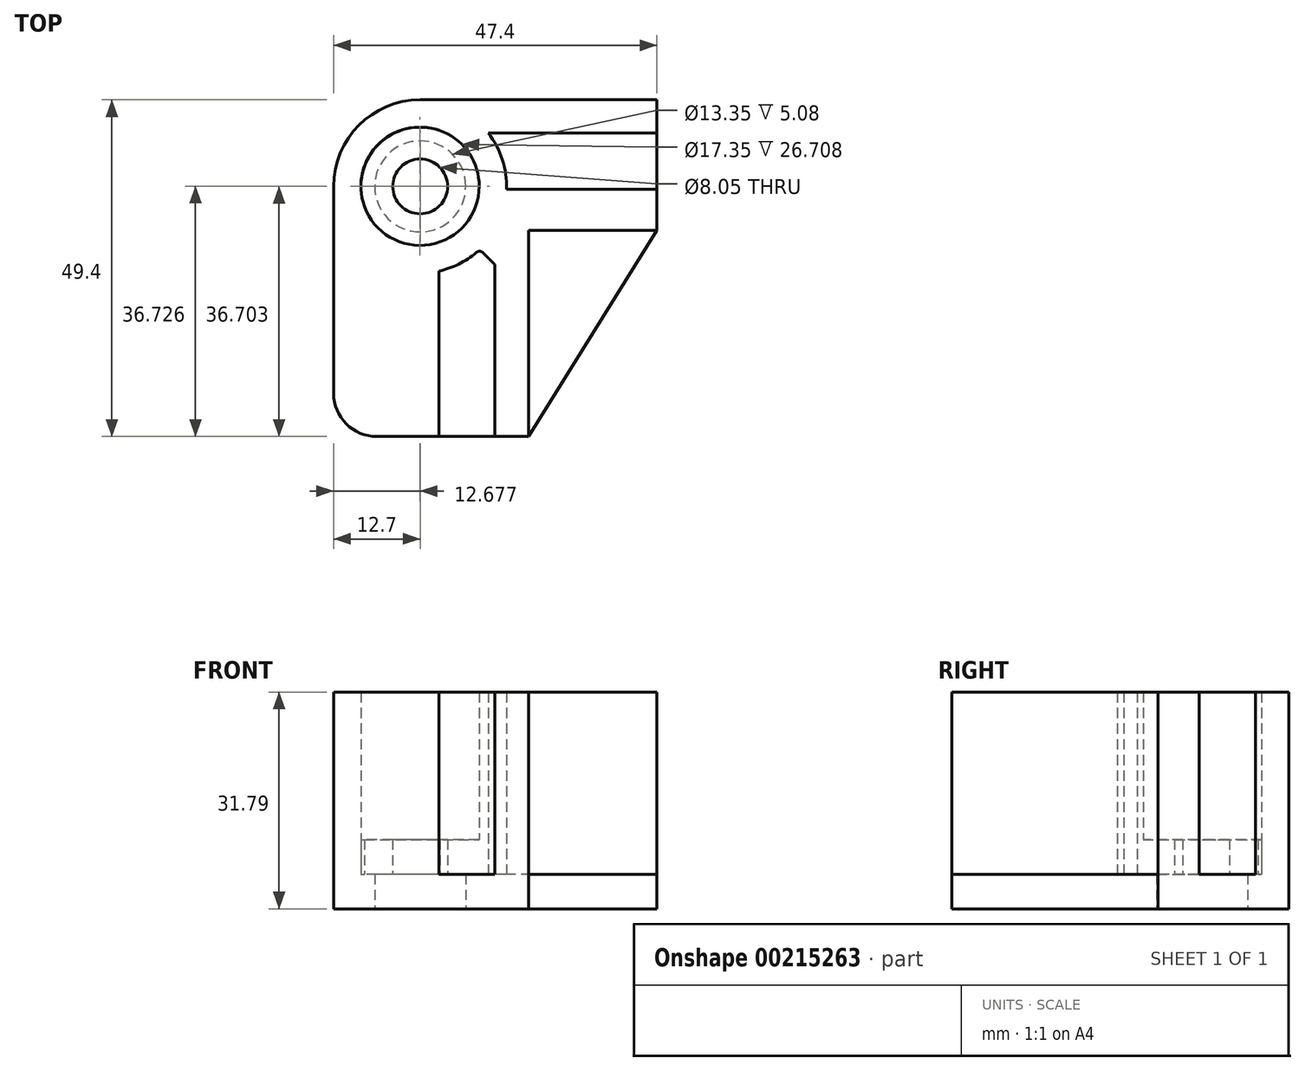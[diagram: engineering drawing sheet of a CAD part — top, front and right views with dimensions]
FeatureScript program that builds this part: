
annotation { "Feature Type Name" : "Feature", "Feature Type Description" : "" }
export const myFeature = defineFeature(function(context is Context, id is Id, definition is map)
    precondition{}
    {
        {
            var Q0;
            Q0=qCreatedBy(makeId("Top.planeOp"),FACE);
            var sketch = newSketch(context, id + "F0", { "sketchPlane" : qUnion([Q0])});
            skLineSegment(sketch, "E0.bottom", {"start": v(6.35, 0) * mm, "end": v(28.6, 0) * mm});
            skLineSegment(sketch, "E0.top", {"start": v(12.7, 49.4) * mm, "end": v(47.4, 49.4) * mm});
            skLineSegment(sketch, "E0.left", {"start": v(0, 6.35) * mm, "end": v(0, 36.7) * mm});
            skLineSegment(sketch, "E0.right", {"start": v(47.4, 30.23) * mm, "end": v(47.4, 49.4) * mm});
            skPoint(sketch, "E1", {"position": v(47.4, 30.23) * mm});
            skPoint(sketch, "E2", {"position": v(28.6, 0) * mm});
            skLineSegment(sketch, "E3", {"start": v(28.6, 0) * mm, "end": v(47.4, 30.23) * mm});
            skArc(sketch, "E4.filletArc", {"start": v(12.7, 49.4) * mm, "mid": v(3.72, 45.68) * mm, "end": v(0, 36.7) * mm});
            skArc(sketch, "E5.filletArc", {"start": v(0, 6.35) * mm, "mid": v(1.86, 1.86) * mm, "end": v(6.35, 0) * mm});
            skCircle(sketch, "E6", {"center": v(12.7, 36.7) * mm, "radius": 6.67 * mm});
            skSolve(sketch);
        }
        {
            var Q0;
            Q0=makeQuery(id+"F0.imprint","IMPRINT",FACE,{"disambiguationData":[TD([[makeQuery(id+"F0.imprint","IMPRINT",EDGE,{"derivedFrom":sQuery(id+"F0.wireOp",EDGE,"E0.bottom")}),1.0]])]});
            extrude(context, id + "F1", {"entities" : qUnion([Q0]), "depth" : 5.08 * mm});
        }
        {
            var Q0;
            Q0=makeQuery(id+"F1.opExtrude","CAP_FACE",FACE,{"disambiguationData":[OSD([sQuery(id+"F0.wireOp",EDGE,"E0.bottom"),sQuery(id+"F0.wireOp",EDGE,"E0.top"),sQuery(id+"F0.wireOp",EDGE,"E0.left"),sQuery(id+"F0.wireOp",EDGE,"E0.right"),sQuery(id+"F0.wireOp",EDGE,"E3"),sQuery(id+"F0.wireOp",EDGE,"E4.filletArc"),sQuery(id+"F0.wireOp",EDGE,"E5.filletArc"),sQuery(id+"F0.wireOp",EDGE,"E6")])],"isStart":false});
            var Q1;
            Q1=makeQuery(id+"F1.opExtrude","CAP_FACE",FACE,{"disambiguationData":[OSD([sQuery(id+"F0.wireOp",EDGE,"E0.bottom"),sQuery(id+"F0.wireOp",EDGE,"E0.top"),sQuery(id+"F0.wireOp",EDGE,"E0.left"),sQuery(id+"F0.wireOp",EDGE,"E0.right"),sQuery(id+"F0.wireOp",EDGE,"E3"),sQuery(id+"F0.wireOp",EDGE,"E4.filletArc"),sQuery(id+"F0.wireOp",EDGE,"E5.filletArc"),sQuery(id+"F0.wireOp",EDGE,"E6")])],"isStart":false});
            var Q2;
            Q2=qCreatedBy(makeId("Front.planeOp"),FACE);
            var sketch = newSketch(context, id + "F2", { "sketchPlane" : qUnion([Q0, Q1, Q2])});
            skLineSegment(sketch, "E7.bottom", {"start": v(6.35, 0) * mm, "end": v(28.6, 0) * mm});
            skLineSegment(sketch, "E7.top", {"start": v(12.7, 49.4) * mm, "end": v(47.4, 49.4) * mm});
            skLineSegment(sketch, "E7.left", {"start": v(0, 6.36) * mm, "end": v(0, 36.7) * mm});
            skLineSegment(sketch, "E7.right", {"start": v(47.4, 30.23) * mm, "end": v(47.4, 49.4) * mm});
            skPoint(sketch, "E8", {"position": v(47.4, 30.23) * mm});
            skPoint(sketch, "E9", {"position": v(28.6, 0) * mm});
            skLineSegment(sketch, "E10", {"start": v(28.6, 0) * mm, "end": v(47.4, 30.23) * mm});
            skArc(sketch, "E11.filletArc", {"start": v(0, 6.36) * mm, "mid": v(1.86, 1.87) * mm, "end": v(6.35, 0) * mm});
            skCircle(sketch, "E12", {"center": v(12.68, 36.73) * mm, "radius": 4.38 * mm});
            skArc(sketch, "E13", {"start": v(25.35, 36.3) * mm, "mid": v(24.74, 40.64) * mm, "end": v(22.68, 44.51) * mm});
            skCircle(sketch, "E14", {"center": v(12.68, 36.73) * mm, "radius": 8.67 * mm});
            skPoint(sketch, "E15", {"position": v(47.4, 44.51) * mm});
            skLineSegment(sketch, "E16", {"start": v(47.4, 44.51) * mm, "end": v(22.68, 44.51) * mm});
            skPoint(sketch, "E17", {"position": v(47.4, 36.3) * mm});
            skLineSegment(sketch, "E18", {"start": v(47.4, 36.3) * mm, "end": v(25.35, 36.3) * mm});
            skLineSegment(sketch, "E19", {"start": v(47.4, 30.23) * mm, "end": v(28.6, 30.23) * mm});
            skLineSegment(sketch, "E20", {"start": v(28.6, 0) * mm, "end": v(28.6, 30.23) * mm});
            skLineSegment(sketch, "E21.0", {"start": v(23.65, 0) * mm, "end": v(23.65, 25.25) * mm});
            skLineSegment(sketch, "E22.0", {"start": v(15.43, 0) * mm, "end": v(15.43, 24.35) * mm});
            skLineSegment(sketch, "E23.0", {"start": v(9.46, 0) * mm, "end": v(9.46, 24.46) * mm});
            skLineSegment(sketch, "E24.0", {"start": v(47.4, 32.04) * mm, "end": v(47.4, 43.05) * mm});
            skArc(sketch, "E25.trimOffspring", {"start": v(12.7, 49.4) * mm, "mid": v(3.71, 45.69) * mm, "end": v(0, 36.7) * mm});
            skArc(sketch, "E26", {"start": v(0, 35.37) * mm, "mid": v(3.02, 28.4) * mm, "end": v(9.46, 24.39) * mm});
            skLineSegment(sketch, "E27.trimOffspring", {"start": v(23.65, 30.23) * mm, "end": v(23.56, 30.23) * mm});
            skArc(sketch, "E28.trimOffspring", {"start": v(15.43, 24.28) * mm, "mid": v(18.35, 25.3) * mm, "end": v(20.93, 27) * mm});
            skLineSegment(sketch, "E29", {"start": v(23.65, 25.25) * mm, "end": v(21.94, 26.97) * mm});
            skArc(sketch, "E30.filletArc", {"start": v(21.94, 26.97) * mm, "mid": v(21.44, 27.19) * mm, "end": v(20.93, 27) * mm});
            skLineSegment(sketch, "E31.trimOffspring", {"start": v(23.65, 30.23) * mm, "end": v(23.65, 30.23) * mm});
            skSolve(sketch);
        }
        {
            var Q0;
            {var subQ2=sQuery(id+"F2.wireOp",EDGE,"E13");Q0=makeQuery(id+"F2.imprint","IMPRINT",FACE,{"disambiguationData":[TD([[makeQuery(id+"F2.imprint","IMPRINT",EDGE,{"derivedFrom":subQ2}),1.0]])]});}
            extrude(context, id + "F3", {"entities" : qUnion([Q0]), "operationType" : NewBodyOperationType.ADD, "depth" : 21.63 * mm});
        }
        {
            var Q0;
            {var subQ0=sQuery(id+"F0.wireOp",EDGE,"E6");Q0=makeQuery(id+"F3.boolean.opBoolean","SPLIT",FACE,{"disambiguationData":[TD([makeQuery(id+"F1.opExtrude","SWEPT_FACE",FACE,{"disambiguationData":[OSD([subQ0])]})])],"derivedFrom":makeQuery(id+"F1.opExtrude","CAP_FACE",FACE,{"disambiguationData":[OSD([sQuery(id+"F0.wireOp",EDGE,"E0.bottom"),sQuery(id+"F0.wireOp",EDGE,"E0.top"),sQuery(id+"F0.wireOp",EDGE,"E0.left"),sQuery(id+"F0.wireOp",EDGE,"E0.right"),sQuery(id+"F0.wireOp",EDGE,"E3"),sQuery(id+"F0.wireOp",EDGE,"E4.filletArc"),sQuery(id+"F0.wireOp",EDGE,"E5.filletArc"),subQ0])],"isStart":false})});}
            var sketch = newSketch(context, id + "F4", { "sketchPlane" : qUnion([Q0])});
            skCircle(sketch, "E32", {"center": v(12.7, 36.7) * mm, "radius": 4.02 * mm});
            skCircle(sketch, "E33", {"center": v(12.7, 36.7) * mm, "radius": 8.69 * mm});
            skSolve(sketch);
        }
        {
            var Q0;
            Q0=makeQuery(id+"F4.imprint","IMPRINT",FACE,{"disambiguationData":[TD([[makeQuery(id+"F4.imprint","IMPRINT",EDGE,{"derivedFrom":sQuery(id+"F4.wireOp",EDGE,"E32")}),-1.0]])]});
            var Q1;
            Q1=makeQuery(id+"F4.imprint","IMPRINT",FACE,{"disambiguationData":[TD([[makeQuery(id+"F4.imprint","IMPRINT",EDGE,{"derivedFrom":makeQuery(id+"F1.opExtrude","CAP_EDGE",EDGE,{"disambiguationData":[OSD([sQuery(id+"F0.wireOp",EDGE,"E6")])],"isStart":false})}),-1.0]])]});
            extrude(context, id + "F5", {"entities" : qUnion([Q0, Q1]), "operationType" : NewBodyOperationType.ADD, "depth" : 5.08 * mm});
        }
        {
            var Q0;
            Q0=makeQuery(id+"F3.opExtrude","CAP_FACE",FACE,{"disambiguationData":[OSD([sQuery(id+"F0.wireOp",EDGE,"E0.right"),sQuery(id+"F0.wireOp",EDGE,"E4.filletArc"),sQuery(id+"F2.wireOp",EDGE,"E7.bottom"),sQuery(id+"F2.wireOp",EDGE,"E7.top"),sQuery(id+"F2.wireOp",EDGE,"E7.left"),sQuery(id+"F2.wireOp",EDGE,"E13"),sQuery(id+"F2.wireOp",EDGE,"E14"),sQuery(id+"F2.wireOp",EDGE,"E16"),sQuery(id+"F2.wireOp",EDGE,"E18"),sQuery(id+"F2.wireOp",EDGE,"E19"),sQuery(id+"F2.wireOp",EDGE,"E20"),sQuery(id+"F2.wireOp",EDGE,"E21.0"),sQuery(id+"F2.wireOp",EDGE,"E22.0"),sQuery(id+"F2.wireOp",EDGE,"E23.0"),sQuery(id+"F2.wireOp",EDGE,"E24.0"),sQuery(id+"F2.wireOp",EDGE,"E26"),sQuery(id+"F2.wireOp",EDGE,"E28.trimOffspring"),sQuery(id+"F2.wireOp",EDGE,"E29"),sQuery(id+"F2.wireOp",EDGE,"E30.filletArc")])],"isStart":false});
            extrude(context, id + "F6", {"entities" : qUnion([Q0]), "operationType" : NewBodyOperationType.ADD, "depth" : 5.08 * mm, "offsetDistance" : 25.4 * mm});
        }
        {
            var Q0;
            {var subQ2=sQuery(id+"F0.wireOp",EDGE,"E5.filletArc");var subQ3=sQuery(id+"F0.wireOp",EDGE,"E0.left");var subQ4=sQuery(id+"F0.wireOp",EDGE,"E0.bottom");Q0=makeQuery(id+"F3.boolean.opBoolean","SPLIT",FACE,{"disambiguationData":[TD([makeQuery(id+"F1.opExtrude","SWEPT_FACE",FACE,{"disambiguationData":[OSD([subQ3])]})])],"derivedFrom":makeQuery(id+"F1.opExtrude","CAP_FACE",FACE,{"disambiguationData":[OSD([subQ4,sQuery(id+"F0.wireOp",EDGE,"E0.top"),subQ3,sQuery(id+"F0.wireOp",EDGE,"E0.right"),sQuery(id+"F0.wireOp",EDGE,"E3"),sQuery(id+"F0.wireOp",EDGE,"E4.filletArc"),subQ2,sQuery(id+"F0.wireOp",EDGE,"E6")])],"isStart":false})});}
            var Q1;
            Q1=makeQuery(id+"F6.opExtrude","CAP_FACE",FACE,{"disambiguationData":[OSD([sQuery(id+"F0.wireOp",EDGE,"E0.right"),sQuery(id+"F0.wireOp",EDGE,"E4.filletArc"),sQuery(id+"F2.wireOp",EDGE,"E7.bottom"),sQuery(id+"F2.wireOp",EDGE,"E7.top"),sQuery(id+"F2.wireOp",EDGE,"E7.left"),sQuery(id+"F2.wireOp",EDGE,"E13"),sQuery(id+"F2.wireOp",EDGE,"E14"),sQuery(id+"F2.wireOp",EDGE,"E16"),sQuery(id+"F2.wireOp",EDGE,"E18"),sQuery(id+"F2.wireOp",EDGE,"E19"),sQuery(id+"F2.wireOp",EDGE,"E20"),sQuery(id+"F2.wireOp",EDGE,"E21.0"),sQuery(id+"F2.wireOp",EDGE,"E22.0"),sQuery(id+"F2.wireOp",EDGE,"E23.0"),sQuery(id+"F2.wireOp",EDGE,"E24.0"),sQuery(id+"F2.wireOp",EDGE,"E26"),sQuery(id+"F2.wireOp",EDGE,"E28.trimOffspring"),sQuery(id+"F2.wireOp",EDGE,"E29"),sQuery(id+"F2.wireOp",EDGE,"E30.filletArc")])],"isStart":false});
            extrude(context, id + "F7", {"entities" : qUnion([Q0]), "operationType" : NewBodyOperationType.ADD, "endBound" : BoundingType.UP_TO_SURFACE, "depth" : 25.4 * mm, "endBoundEntityFace" : qUnion([Q1]), "offsetDistance" : 25.4 * mm});
        }
    });
